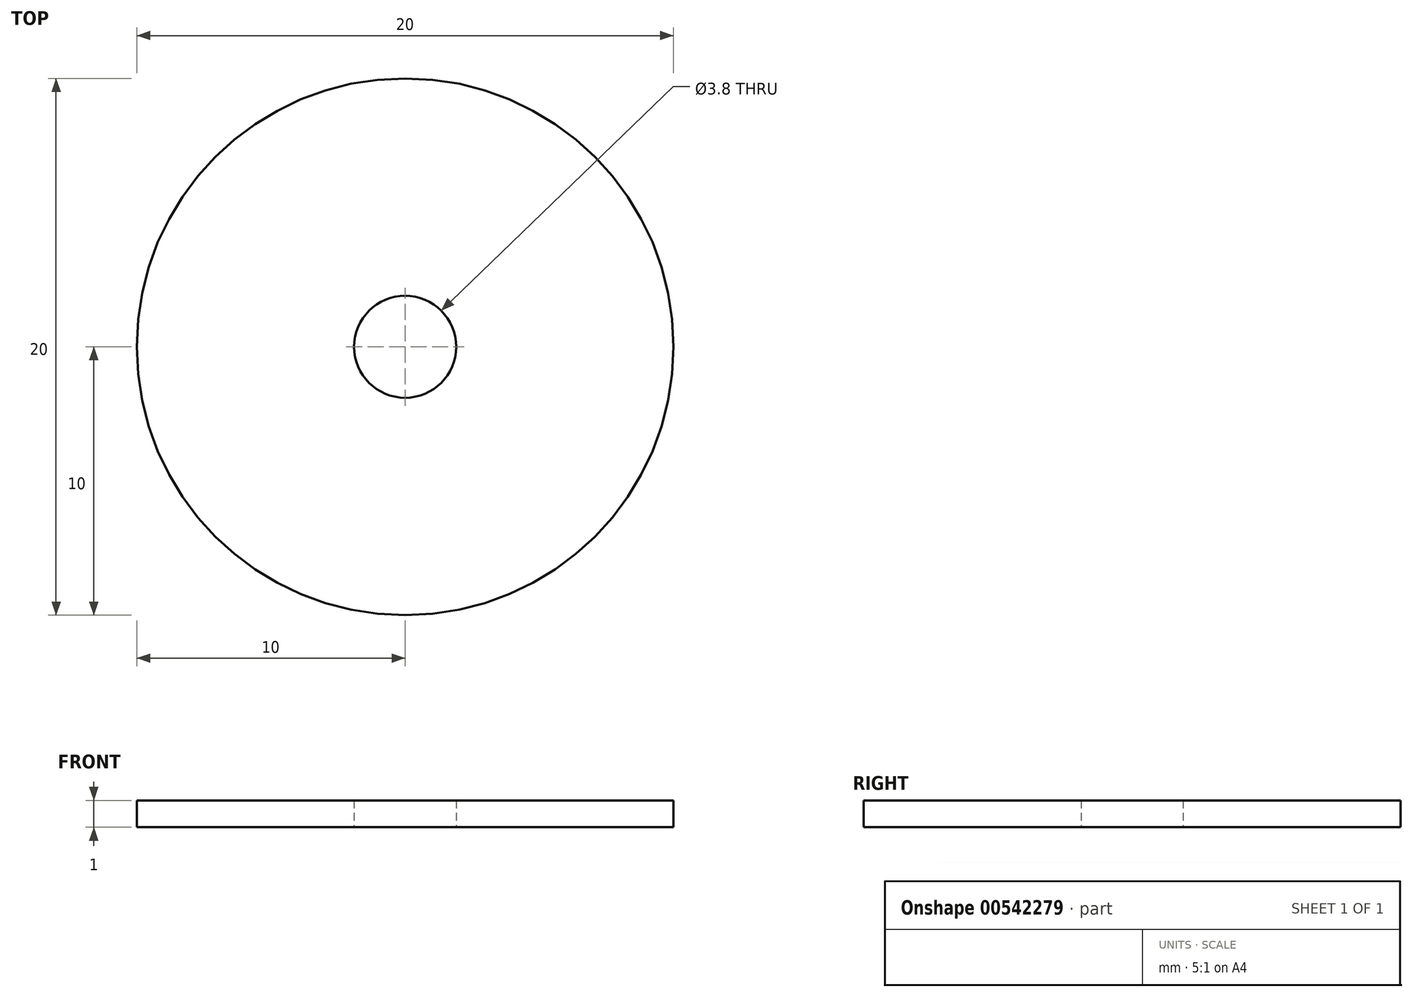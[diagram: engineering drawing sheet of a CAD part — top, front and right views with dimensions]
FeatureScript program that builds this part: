
annotation { "Feature Type Name" : "Feature", "Feature Type Description" : "" }
export const myFeature = defineFeature(function(context is Context, id is Id, definition is map)
    precondition{}
    {
        {
            var Q0;
            Q0=qCreatedBy(makeId("Top.planeOp"),FACE);
            var sketch = newSketch(context, id + "F0", { "sketchPlane" : qUnion([Q0])});
            skCircle(sketch, "E0", {"center": v(0, 0) * mm, "radius": 10 * mm});
            skCircle(sketch, "E1", {"center": v(0, 0) * mm, "radius": 1.9 * mm});
            skSolve(sketch);
        }
        {
            var Q0;
            Q0=makeQuery(id+"F0.imprint","IMPRINT",FACE,{"disambiguationData":[TD([[makeQuery(id+"F0.imprint","IMPRINT",EDGE,{"derivedFrom":sQuery(id+"F0.wireOp",EDGE,"E0")}),1.0]])]});
            extrude(context, id + "F1", {"entities" : qUnion([Q0]), "depth" : 1 * mm, "offsetDistance" : 25 * mm});
        }
    });
